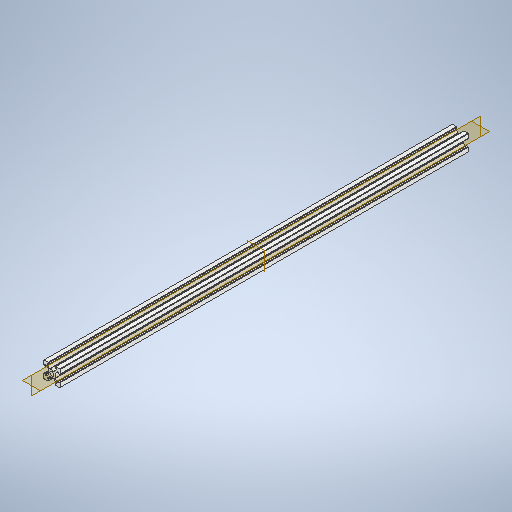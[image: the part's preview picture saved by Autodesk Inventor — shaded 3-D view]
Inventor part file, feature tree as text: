
AUTODESK INVENTOR PART (.ipt)
format: ipt  version: 2025.2 (Build 292293000, 293)  size: 356,864 bytes
history: native  units: mm
features: mirror x2, other x1, extrude x1, sketch x1
ambient origin geometry x8: Origin, YZ Plane, XZ Plane, XY Plane, X Axis, Y Axis, Z Axis, Center Point
bodies: Body1 (feature_tree)
feature tree (5):
  other  "Sólido1"
  extrude  "Extrusão1"  Depth=5.0mm
  mirror  "Espelhar1"
  mirror  "Espelhar2"
  sketch  "Esboço1"  dims[d0=20.0mm d2=5.0mm d3=6.0mm d5=2.0mm d7=1.0mm d8=6.0mm d9=1.0mm d10=0.5mm d11=0.5mm d12=0.5mm d14=0.5mm d15=0.5mm d16=10.0mm d17=2.5mm d18=500.0mm d19=0.0mm d20=0.5mm d21=0.5mm]
